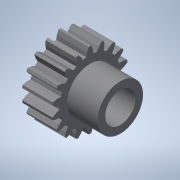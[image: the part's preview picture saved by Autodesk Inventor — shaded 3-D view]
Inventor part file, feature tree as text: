
AUTODESK INVENTOR PART (.ipt)
format: ipt  version: 2020.2 (Build 242310000, 310)  size: 234,496 bytes
history: native  units: mm
features: hole x1, imported_body x1, sketch x1
ambient origin geometry x8: Origin, YZ Plane, XZ Plane, XY Plane, X Axis, Y Axis, Z Axis, Center Point
bodies: Body1 (feature_tree)
feature tree (3):
  hole  "Bohrung1"  [1 undecoded]
  imported_body  "Basis1"
  sketch  "Skizze1"  dims[d0=4.0mm d1=6.0mm d2=4.0mm d3=2.0mm d4=90.0deg d5=8.0mm d6=20.594885mm]
note: 1 required parameter value undecoded (feature->parameter linkage not recoverable at this tier; creation-order binding heuristic only, values carry confidence <= 0.55)
